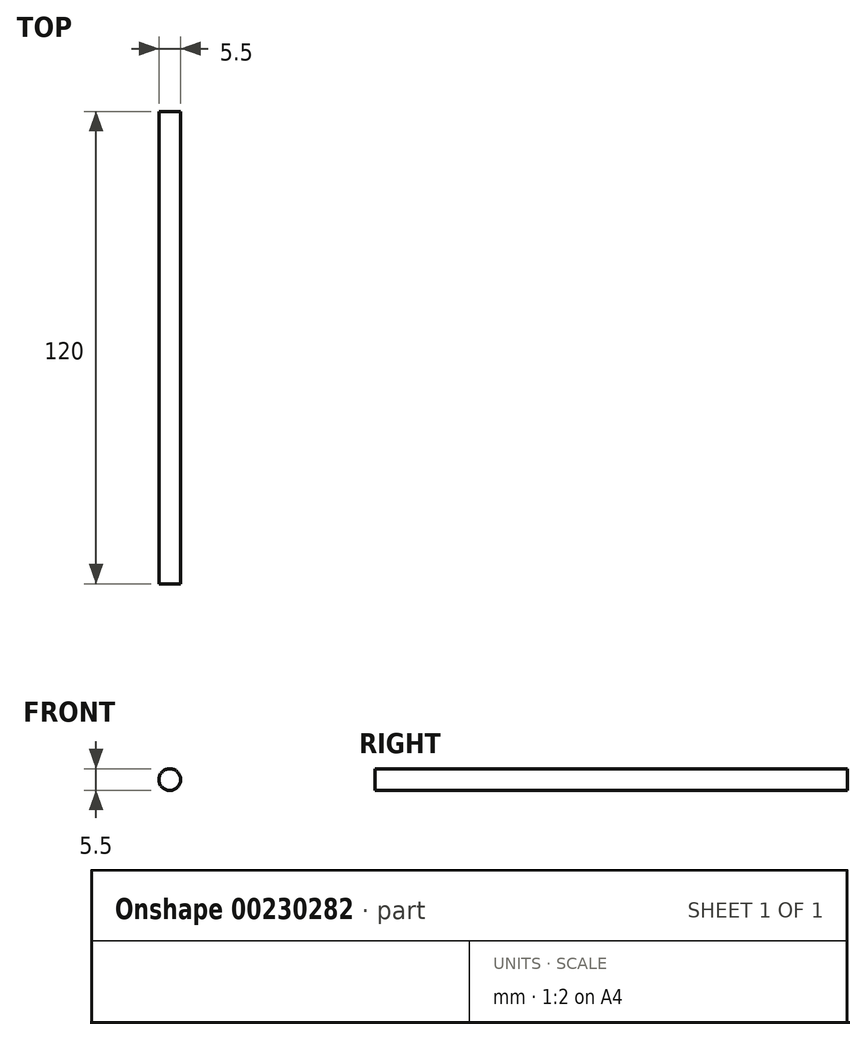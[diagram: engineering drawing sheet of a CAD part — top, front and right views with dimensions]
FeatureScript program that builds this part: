
annotation { "Feature Type Name" : "Feature", "Feature Type Description" : "" }
export const myFeature = defineFeature(function(context is Context, id is Id, definition is map)
    precondition{}
    {
        {
            var Q0;
            Q0=qCreatedBy(makeId("Front.planeOp"),FACE);
            var sketch = newSketch(context, id + "F0", { "sketchPlane" : qUnion([Q0])});
            skCircle(sketch, "E0", {"center": v(0, 0) * mm, "radius": 2.75 * mm});
            skSolve(sketch);
        }
        {
            var Q0;
            Q0=makeQuery(id+"F0.imprint","IMPRINT",FACE,{"disambiguationData":[TD([[makeQuery(id+"F0.imprint","IMPRINT",EDGE,{"derivedFrom":sQuery(id+"F0.wireOp",EDGE,"E0")}),1.0]])]});
            extrude(context, id + "F1", {"entities" : qUnion([Q0]), "endBound" : BoundingType.SYMMETRIC, "depth" : 120 * mm});
        }
    });
